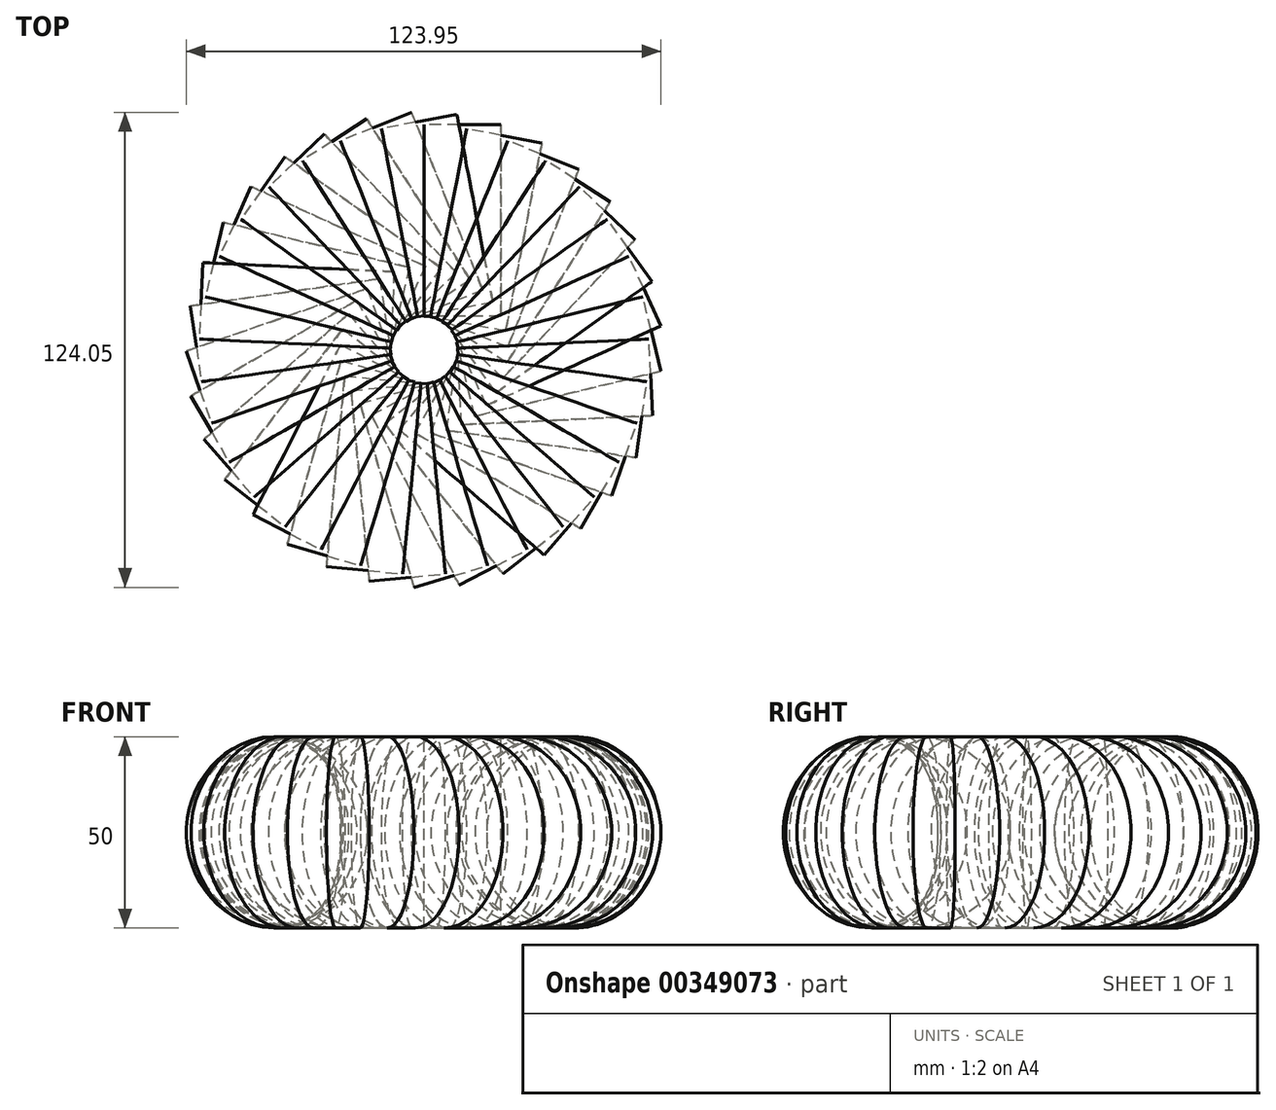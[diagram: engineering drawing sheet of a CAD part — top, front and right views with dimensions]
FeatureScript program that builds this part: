
annotation { "Feature Type Name" : "Feature", "Feature Type Description" : "" }
export const myFeature = defineFeature(function(context is Context, id is Id, definition is map)
    precondition{}
    {
        {
            var Q0;
            Q0=qCreatedBy(makeId("Front.planeOp"),FACE);
            var sketch = newSketch(context, id + "F0", { "sketchPlane" : qUnion([Q0])});
            skLineSegment(sketch, "E0", {"start": v(0, 72.63) * mm, "end": v(0, -67.58) * mm, "construction": true});
            skSolve(sketch);
        }
        {
            var Q0;
            Q0=qCreatedBy(makeId("Right.planeOp"),FACE);
            var sketch = newSketch(context, id + "F1", { "sketchPlane" : qUnion([Q0])});
            skCircle(sketch, "E1", {"center": v(33.8, 33.8) * mm, "radius": 25 * mm});
            skSolve(sketch);
        }
        {
            var Q0;
            Q0 = qSketchRegion(id + "F1", true);
            extrude(context, id + "F2", {"entities" : qUnion([Q0]), "depth" : 20 * mm, "offsetDistance" : 25 * mm});
        }
        {
            var Q0;
            Q0=makeQuery(id+"F2.opExtrude","SWEPT_BODY",BODY,{"disambiguationData":[OSD([sQuery(id+"F1.wireOp",EDGE,"E1")])]});
            var Q1;
            Q1=sQuery(id+"F0.wireOp",EDGE,"E0");
            circularPattern(context, id + "F3", {"entities" : qUnion([Q0]), "axis" : qUnion([Q1]), "angle" : 360 * degree, "instanceCount" : 33, "equalSpace" : true});
        }
    });
